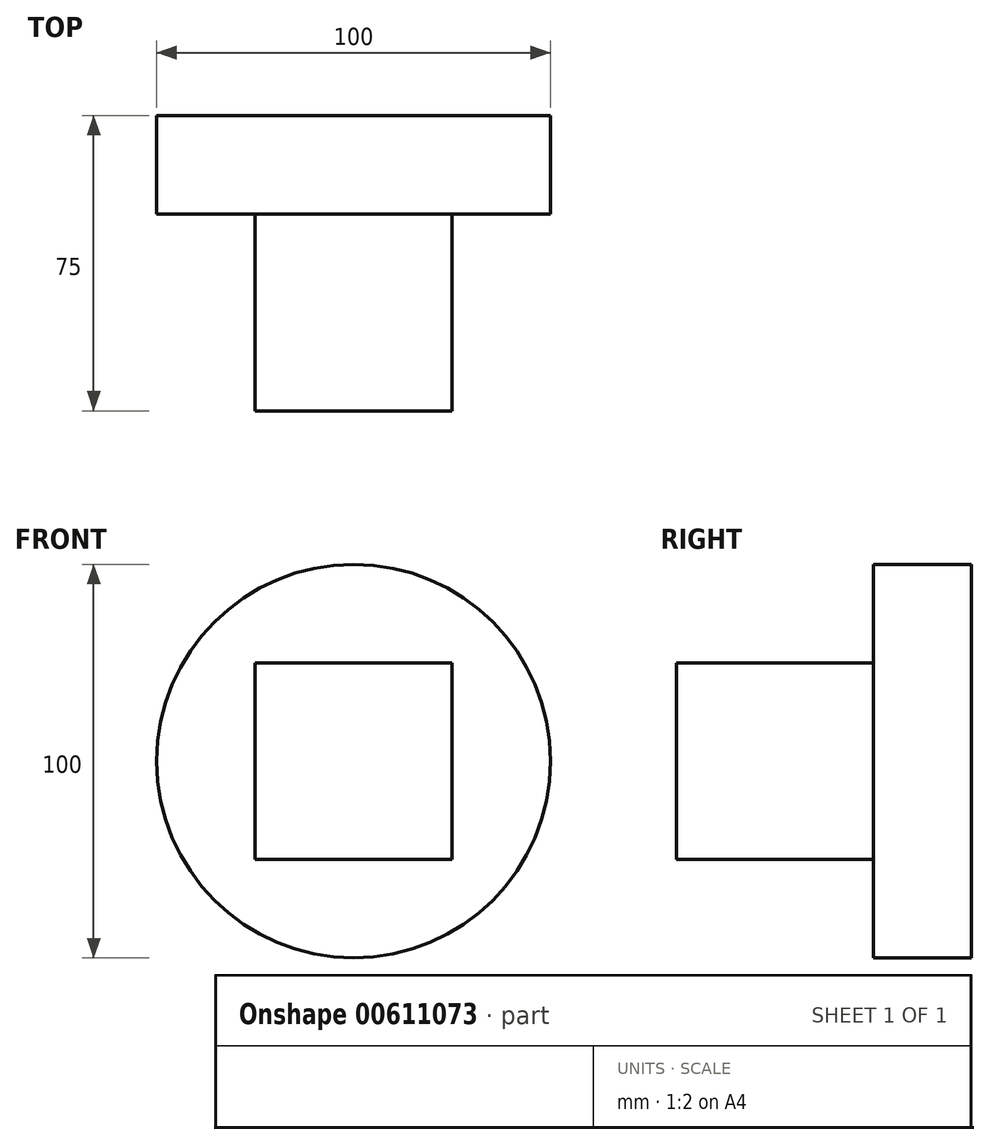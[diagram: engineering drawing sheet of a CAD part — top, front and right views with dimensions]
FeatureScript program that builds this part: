
annotation { "Feature Type Name" : "Feature", "Feature Type Description" : "" }
export const myFeature = defineFeature(function(context is Context, id is Id, definition is map)
    precondition{}
    {
        {
            var Q0;
            Q0=qCreatedBy(makeId("Top.planeOp"),FACE);
            var sketch = newSketch(context, id + "F0", { "sketchPlane" : qUnion([Q0])});
            skLineSegment(sketch, "E0.bottom", {"start": v(-25, 25) * mm, "end": v(25, 25) * mm});
            skLineSegment(sketch, "E0.top", {"start": v(-25, -25) * mm, "end": v(25, -25) * mm});
            skLineSegment(sketch, "E0.left", {"start": v(-25, 25) * mm, "end": v(-25, -25) * mm});
            skLineSegment(sketch, "E0.right", {"start": v(25, 25) * mm, "end": v(25, -25) * mm});
            skPoint(sketch, "E1", {"position": v(0, 25) * mm});
            skPoint(sketch, "E2", {"position": v(-25, 0) * mm});
            skSolve(sketch);
        }
        {
            var Q0;
            Q0 = qSketchRegion(id + "F0", true);
            extrude(context, id + "F1", {"entities" : qUnion([Q0]), "endBound" : BoundingType.SYMMETRIC, "depth" : 50 * mm, "offsetDistance" : 25 * mm});
        }
        {
            var Q0;
            Q0=makeQuery(id+"F1.opExtrude","SWEPT_FACE",FACE,{"disambiguationData":[OSD([sQuery(id+"F0.wireOp",EDGE,"E0.bottom")])]});
            var sketch = newSketch(context, id + "F2", { "sketchPlane" : qUnion([Q0])});
            skCircle(sketch, "E3", {"center": v(0, 0) * mm, "radius": 50 * mm});
            skSolve(sketch);
        }
        {
            var Q0;
            Q0 = qSketchRegion(id + "F2", true);
            extrude(context, id + "F3", {"entities" : qUnion([Q0]), "depth" : 25 * mm, "offsetDistance" : 25 * mm});
        }
    });
